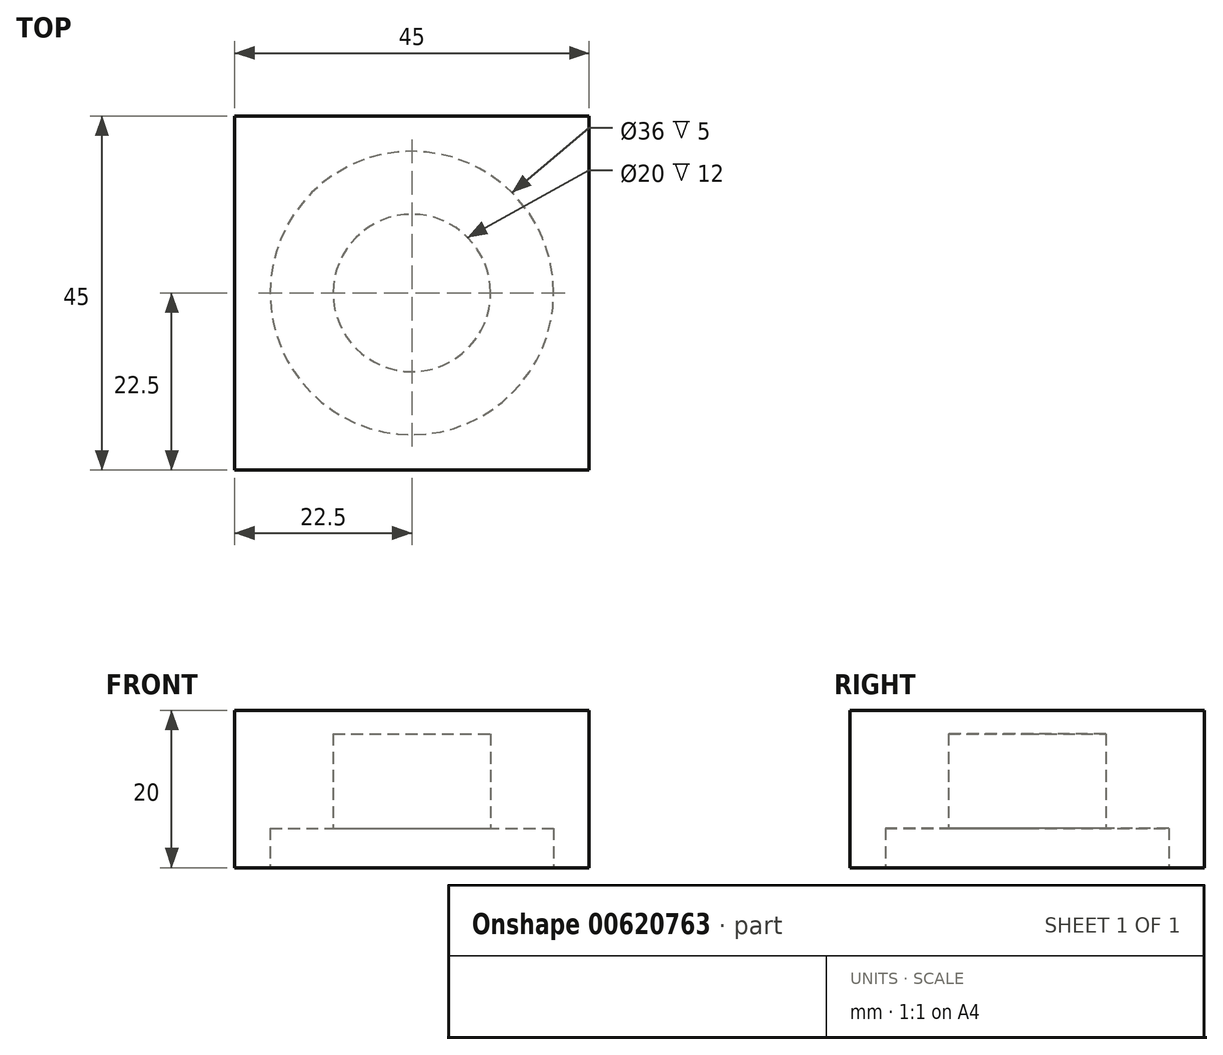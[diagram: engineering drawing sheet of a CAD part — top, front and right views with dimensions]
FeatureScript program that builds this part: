
annotation { "Feature Type Name" : "Feature", "Feature Type Description" : "" }
export const myFeature = defineFeature(function(context is Context, id is Id, definition is map)
    precondition{}
    {
        {
            var Q0;
            Q0=qCreatedBy(makeId("Top.planeOp"),FACE);
            var sketch = newSketch(context, id + "F0", { "sketchPlane" : qUnion([Q0])});
            skLineSegment(sketch, "E0.bottom", {"start": v(22.5, 22.5) * mm, "end": v(-22.5, 22.5) * mm});
            skLineSegment(sketch, "E0.top", {"start": v(22.5, -22.5) * mm, "end": v(-22.5, -22.5) * mm});
            skLineSegment(sketch, "E0.left", {"start": v(22.5, 22.5) * mm, "end": v(22.5, -22.5) * mm});
            skLineSegment(sketch, "E0.right", {"start": v(-22.5, 22.5) * mm, "end": v(-22.5, -22.5) * mm});
            skPoint(sketch, "E0.middle", {"position": v(0, 0) * mm});
            skSolve(sketch);
        }
        {
            var Q0;
            Q0=makeQuery(id+"F0.imprint","IMPRINT",FACE,{"disambiguationData":[TD([[makeQuery(id+"F0.imprint","IMPRINT",EDGE,{"derivedFrom":sQuery(id+"F0.wireOp",EDGE,"E0.bottom")}),1.0]])]});
            extrude(context, id + "F1", {"entities" : qUnion([Q0]), "depth" : 20 * mm, "offsetDistance" : 25 * mm});
        }
        {
            var Q0;
            Q0=makeQuery(id+"F1.opExtrude","CAP_FACE",FACE,{"disambiguationData":[OSD([sQuery(id+"F0.wireOp",EDGE,"E0.bottom"),sQuery(id+"F0.wireOp",EDGE,"E0.top"),sQuery(id+"F0.wireOp",EDGE,"E0.left"),sQuery(id+"F0.wireOp",EDGE,"E0.right")])],"isStart":true});
            var sketch = newSketch(context, id + "F2", { "sketchPlane" : qUnion([Q0])});
            skCircle(sketch, "E1", {"center": v(0, 0) * mm, "radius": 10 * mm});
            skSolve(sketch);
        }
        {
            var Q0;
            Q0=makeQuery(id+"F2.imprint","IMPRINT",FACE,{"disambiguationData":[TD([[makeQuery(id+"F2.imprint","IMPRINT",EDGE,{"derivedFrom":sQuery(id+"F2.wireOp",EDGE,"E1")}),-1.0]])]});
            var sketch = newSketch(context, id + "F3", { "sketchPlane" : qUnion([Q0])});
            skCircle(sketch, "E2", {"center": v(0, 0) * mm, "radius": 18 * mm});
            skSolve(sketch);
        }
        {
            var Q0;
            Q0 = qSketchRegion(id + "F2", true);
            extrude(context, id + "F4", {"entities" : qUnion([Q0]), "operationType" : NewBodyOperationType.REMOVE, "oppositeDirection" : true, "depth" : 17 * mm, "offsetDistance" : 25 * mm});
        }
        {
            var Q0;
            Q0=makeQuery(id+"F3.imprint","IMPRINT",FACE,{"disambiguationData":[TD([[makeQuery(id+"F3.imprint","IMPRINT",EDGE,{"derivedFrom":sQuery(id+"F3.wireOp",EDGE,"E2")}),1.0]])]});
            extrude(context, id + "F5", {"entities" : qUnion([Q0]), "operationType" : NewBodyOperationType.REMOVE, "oppositeDirection" : true, "depth" : 5 * mm, "offsetDistance" : 25 * mm});
        }
    });
